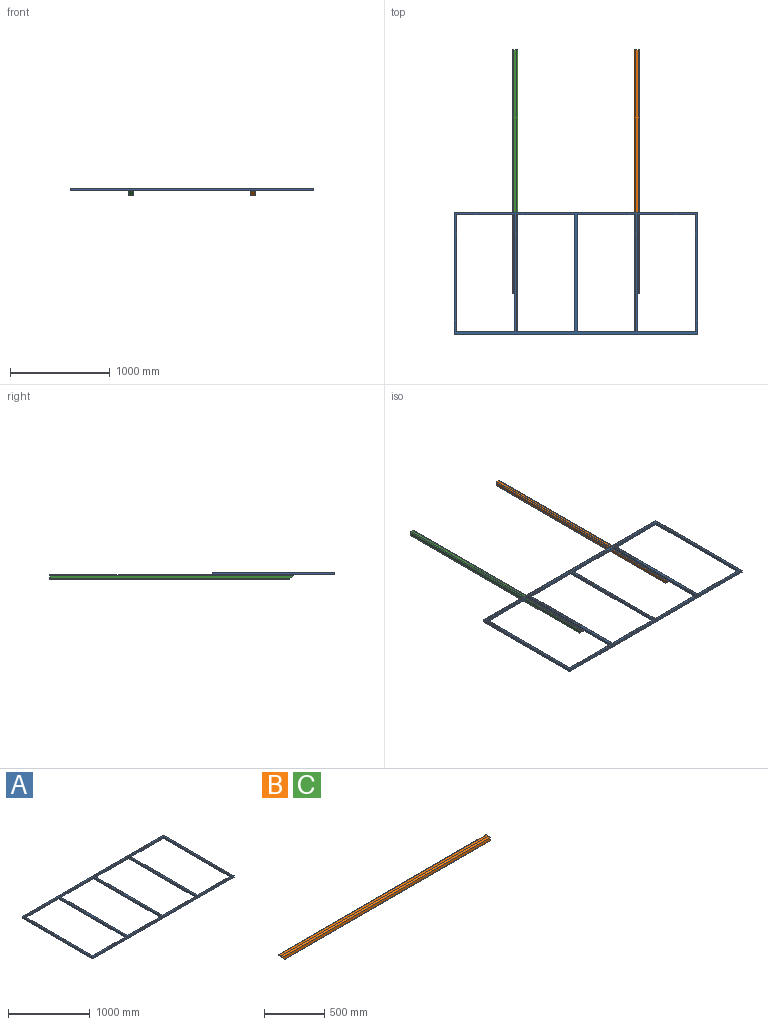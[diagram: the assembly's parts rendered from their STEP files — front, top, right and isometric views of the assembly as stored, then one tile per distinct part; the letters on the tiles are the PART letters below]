
ASSEMBLY  parts=3 mates=2
PART A: 214 faces, bbox 2438.4x1219.2x25.4 mm
  f0: plane 2438.4x22.86mm, normal (0,-1,0), area 55741.8mm2, adj f1,f2,f34,f43
  f1: cylinder r=1.28mm len=2438.4mm, axis (1,0,0), area 4848.5mm2, adj f0,f35,f42,f52
  f2: cylinder r=1.28mm len=2438.4mm, axis (1,0,0), area 4848.5mm2, adj f0,f33,f44,f45
  f3: plane 577.85x22.86mm, normal (0,1,0), area 13209.7mm2, adj f7,f11,f29,f37
  f4: plane 577.85x22.86mm, normal (0,1,0), area 13209.7mm2, adj f8,f12,f32,f40
  f5: plane 577.85x22.86mm, normal (0,1,0), area 13209.7mm2, adj f9,f14,f23,f26
  f6: plane 577.85x22.86mm, normal (0,1,0), area 13209.7mm2, adj f10,f13,f17,f20
  f7: cylinder r=1.28mm len=580.39mm, axis (1,0,0), area 1151.3mm2, adj f3,f28,f36,f52
  f8: cylinder r=1.28mm len=580.39mm, axis (1,0,0), area 1151.3mm2, adj f4,f30,f41,f52
  f9: cylinder r=1.28mm len=580.39mm, axis (1,0,0), area 1151.3mm2, adj f5,f22,f24,f52
  f10: cylinder r=1.28mm len=580.39mm, axis (1,0,0), area 1151.3mm2, adj f6,f16,f18,f52
  f11: cylinder r=1.28mm len=580.39mm, axis (1,0,0), area 1151.3mm2, adj f3,f27,f38,f45
  f12: cylinder r=1.28mm len=580.39mm, axis (1,0,0), area 1151.3mm2, adj f4,f31,f39,f45
  f13: cylinder r=1.28mm len=580.39mm, axis (1,0,0), area 1151.3mm2, adj f6,f15,f19,f45
  f14: cylinder r=1.28mm len=580.39mm, axis (1,0,0), area 1151.3mm2, adj f5,f21,f25,f45
  f15: cylinder r=1.28mm len=1170.94mm, axis (0,-1,0), area 2326mm2, adj f13,f17,f45,f46
  f16: cylinder r=1.28mm len=1170.94mm, axis (0,-1,0), area 2326mm2, adj f10,f17,f47,f52
  f17: plane 1168.4x22.86mm, normal (-1,0,0), area 26709.6mm2, adj f6,f15,f16,f48
  f18: cylinder r=1.28mm len=1170.94mm, axis (0,1,0), area 2326mm2, adj f10,f20,f47,f52
  f19: cylinder r=1.28mm len=1170.94mm, axis (0,1,0), area 2326mm2, adj f13,f20,f45,f46
  f20: plane 1168.4x22.86mm, normal (1,0,0), area 26709.6mm2, adj f6,f18,f19,f48
  f21: cylinder r=1.28mm len=1170.94mm, axis (0,1,0), area 2326mm2, adj f14,f23,f45,f50
  f22: cylinder r=1.28mm len=1170.94mm, axis (0,1,0), area 2326mm2, adj f9,f23,f49,f52
  f23: plane 1168.4x22.86mm, normal (-1,0,0), area 26709.6mm2, adj f5,f21,f22,f51
  f24: cylinder r=1.28mm len=1170.94mm, axis (0,-1,0), area 2326mm2, adj f9,f26,f49,f52
  f25: cylinder r=1.28mm len=1170.94mm, axis (0,-1,0), area 2326mm2, adj f14,f26,f45,f50
  f26: plane 1168.4x22.86mm, normal (1,0,0), area 26709.6mm2, adj f5,f24,f25,f51
  f27: cylinder r=1.28mm len=1170.94mm, axis (0,-1,0), area 2326mm2, adj f11,f29,f45,f53
  f28: cylinder r=1.28mm len=1170.94mm, axis (0,-1,0), area 2326mm2, adj f7,f29,f52,f54
  f29: plane 1168.4x22.86mm, normal (-1,0,0), area 26709.6mm2, adj f3,f27,f28,f55
  f30: cylinder r=1.28mm len=1170.94mm, axis (0,-1,0), area 2326mm2, adj f8,f32,f52,f59
  f31: cylinder r=1.28mm len=1170.94mm, axis (0,-1,0), area 2326mm2, adj f12,f32,f45,f60
  f32: plane 1168.4x22.86mm, normal (1,0,0), area 26709.6mm2, adj f4,f30,f31,f61
  f33: cylinder r=1.28mm len=1219.2mm, axis (0,-1,0), area 2423.3mm2, adj f2,f34,f45,f56
  f34: plane 1219.2x22.86mm, normal (-1,0,0), area 27870.9mm2, adj f0,f33,f35,f57
  f35: cylinder r=1.28mm len=1219.2mm, axis (0,-1,0), area 2423.3mm2, adj f1,f34,f52,f58
  f36: cylinder r=1.28mm len=1170.94mm, axis (0,-1,0), area 2326mm2, adj f7,f37,f52,f54
  f37: plane 1168.4x22.86mm, normal (1,0,0), area 26709.6mm2, adj f3,f36,f38,f55
  f38: cylinder r=1.28mm len=1170.94mm, axis (0,-1,0), area 2326mm2, adj f11,f37,f45,f53
  f39: cylinder r=1.28mm len=1170.94mm, axis (0,1,0), area 2326mm2, adj f12,f40,f45,f60
  f40: plane 1168.4x22.86mm, normal (-1,0,0), area 26709.6mm2, adj f4,f39,f41,f61
  f41: cylinder r=1.28mm len=1170.94mm, axis (0,1,0), area 2326mm2, adj f8,f40,f52,f59
  f42: cylinder r=1.28mm len=1219.2mm, axis (0,1,0), area 2423.3mm2, adj f1,f43,f52,f58
  f43: plane 1219.2x22.86mm, normal (1,0,0), area 27870.9mm2, adj f0,f42,f44,f57
  f44: cylinder r=1.28mm len=1219.2mm, axis (0,1,0), area 2423.3mm2, adj f2,f43,f45,f56
  f45: plane 2435.86x1216.66mm, normal (0,0,-1), area 245206mm2, adj f2,f11,f12,f13,f14,f15,f19,f21
  f46: cylinder r=1.28mm len=580.39mm, axis (-1,0,0), area 1151.3mm2, adj f15,f19,f45,f48
  f47: cylinder r=1.28mm len=580.39mm, axis (-1,0,0), area 1151.3mm2, adj f16,f18,f48,f52
  f48: plane 577.85x22.86mm, normal (0,-1,0), area 13209.7mm2, adj f17,f20,f46,f47
  f49: cylinder r=1.28mm len=580.39mm, axis (-1,0,0), area 1151.3mm2, adj f22,f24,f51,f52
  f50: cylinder r=1.28mm len=580.39mm, axis (-1,0,0), area 1151.3mm2, adj f21,f25,f45,f51
  f51: plane 577.85x22.86mm, normal (0,-1,0), area 13209.7mm2, adj f23,f26,f49,f50
  f52: plane 2435.86x1216.66mm, normal (0,0,1), area 245206mm2, adj f1,f7,f8,f9,f10,f16,f18,f22
  f53: cylinder r=1.28mm len=580.39mm, axis (-1,0,0), area 1151.3mm2, adj f27,f38,f45,f55
  f54: cylinder r=1.28mm len=580.39mm, axis (-1,0,0), area 1151.3mm2, adj f28,f36,f52,f55
  f55: plane 577.85x22.86mm, normal (0,-1,0), area 13209.7mm2, adj f29,f37,f53,f54
  f56: cylinder r=1.28mm len=2438.4mm, axis (-1,0,0), area 4848.5mm2, adj f33,f44,f45,f57
  f57: plane 2438.4x22.86mm, normal (0,1,0), area 55741.8mm2, adj f34,f43,f56,f58
  f58: cylinder r=1.28mm len=2438.4mm, axis (-1,0,0), area 4848.5mm2, adj f35,f42,f52,f57
  f59: cylinder r=1.28mm len=580.39mm, axis (-1,0,0), area 1151.3mm2, adj f30,f41,f52,f61
  f60: cylinder r=1.28mm len=580.39mm, axis (-1,0,0), area 1151.3mm2, adj f31,f39,f45,f61
  f61: plane 577.85x22.86mm, normal (0,-1,0), area 13209.7mm2, adj f32,f40,f59,f60
  f62: plane 21.13x21.13mm, normal (0,1,0), area 445.2mm2, adj f63,f64,f65,f66,f67,f68,f69,f70
  f63: cylinder r=1.28mm len=1168.4mm, axis (0,-1,0), area 2324.1mm2, adj f62,f64,f70,f71
  f64: plane 1168.4x18.59mm, normal (1,0,0), area 21723.8mm2, adj f62,f63,f65,f71
  f65: cylinder r=1.28mm len=1168.4mm, axis (0,-1,0), area 2324.1mm2, adj f62,f64,f66,f71
  f66: plane 1168.4x18.59mm, normal (0,0,-1), area 21723.8mm2, adj f62,f65,f67,f71
  f67: cylinder r=1.28mm len=1168.4mm, axis (0,-1,0), area 2324.1mm2, adj f62,f66,f68,f71
  f68: plane 1168.4x18.59mm, normal (-1,0,0), area 21723.8mm2, adj f62,f67,f69,f71
  f69: cylinder r=1.28mm len=1168.4mm, axis (0,-1,0), area 2324.1mm2, adj f62,f68,f70,f71
  f70: plane 1168.4x18.59mm, normal (0,0,1), area 21723.8mm2, adj f62,f63,f69,f71
  f71: plane 21.13x21.13mm, normal (0,-1,0), area 445.2mm2, adj f63,f64,f65,f66,f67,f68,f69,f70
  f72: plane 21.13x21.13mm, normal (0,1,0), area 445.2mm2, adj f73,f74,f75,f76,f77,f78,f79,f80
  f73: cylinder r=1.28mm len=1168.4mm, axis (0,-1,0), area 2324.1mm2, adj f72,f74,f80,f81
  f74: plane 1168.4x18.59mm, normal (1,0,0), area 21723.8mm2, adj f72,f73,f75,f81
  f75: cylinder r=1.28mm len=1168.4mm, axis (0,-1,0), area 2324.1mm2, adj f72,f74,f76,f81
  f76: plane 1168.4x18.59mm, normal (0,0,-1), area 21723.8mm2, adj f72,f75,f77,f81
  f77: cylinder r=1.28mm len=1168.4mm, axis (0,-1,0), area 2324.1mm2, adj f72,f76,f78,f81
  f78: plane 1168.4x18.59mm, normal (-1,0,0), area 21723.8mm2, adj f72,f77,f79,f81
  f79: cylinder r=1.28mm len=1168.4mm, axis (0,-1,0), area 2324.1mm2, adj f72,f78,f80,f81
  f80: plane 1168.4x18.59mm, normal (0,0,1), area 21723.8mm2, adj f72,f73,f79,f81
  f81: plane 21.13x21.13mm, normal (0,-1,0), area 445.2mm2, adj f73,f74,f75,f76,f77,f78,f79,f80
  f82: plane 21.13x21.13mm, normal (0,1,0), area 445.2mm2, adj f83,f84,f85,f86,f87,f88,f89,f90
  f83: plane 1168.4x18.59mm, normal (0,0,1), area 21723.8mm2, adj f82,f84,f90,f91
  f84: cylinder r=1.28mm len=1168.4mm, axis (0,1,0), area 2324.1mm2, adj f82,f83,f85,f91
  f85: plane 1168.4x18.59mm, normal (1,0,0), area 21723.8mm2, adj f82,f84,f86,f91
  f86: cylinder r=1.28mm len=1168.4mm, axis (0,1,0), area 2324.1mm2, adj f82,f85,f87,f91
  f87: plane 1168.4x18.59mm, normal (0,0,-1), area 21723.8mm2, adj f82,f86,f88,f91
  f88: cylinder r=1.28mm len=1168.4mm, axis (0,1,0), area 2324.1mm2, adj f82,f87,f89,f91
  f89: plane 1168.4x18.59mm, normal (-1,0,0), area 21723.8mm2, adj f82,f88,f90,f91
  f90: cylinder r=1.28mm len=1168.4mm, axis (0,1,0), area 2324.1mm2, adj f82,f83,f89,f91
  f91: plane 21.13x21.13mm, normal (0,-1,0), area 445.2mm2, adj f83,f84,f85,f86,f87,f88,f89,f90
  f92: cylinder r=1.28mm len=1214.93mm, axis (0,1,0), area 2414.9mm2, adj f93,f116,f177,f183
  f93: plane 1214.93x18.59mm, normal (-1,0,0), area 22589mm2, adj f92,f94,f117,f178
  f94: cylinder r=1.28mm len=1214.93mm, axis (0,1,0), area 2414.9mm2, adj f93,f118,f179,f180
  f95: cylinder r=1.28mm len=1175.21mm, axis (0,1,0), area 2334.5mm2, adj f96,f105,f162,f180
  f96: plane 1172.67x18.59mm, normal (1,0,0), area 21803.2mm2, adj f95,f97,f107,f169
  f97: cylinder r=1.28mm len=1175.21mm, axis (0,1,0), area 2334.5mm2, adj f96,f109,f175,f183
  f98: cylinder r=1.28mm len=21.13mm, axis (1,0,0), area 40.2mm2, adj f100,f152,f157,f180
  f99: cylinder r=1.28mm len=577.85mm, axis (1,0,0), area 1149.4mm2, adj f101,f136,f153,f180
  f100: plane 21.13x18.59mm, normal (0,-1,0), area 392.9mm2, adj f98,f102,f151,f156
  f101: plane 577.85x18.59mm, normal (0,-1,0), area 10743.8mm2, adj f99,f103,f136,f153
  f102: cylinder r=1.28mm len=21.13mm, axis (1,0,0), area 40.2mm2, adj f100,f150,f155,f183
  f103: cylinder r=1.28mm len=577.85mm, axis (1,0,0), area 1149.4mm2, adj f101,f136,f153,f183
  f104: cylinder r=1.28mm len=21.13mm, axis (1,0,0), area 40.2mm2, adj f106,f142,f143,f180
  f105: cylinder r=1.28mm len=581.25mm, axis (1,0,0), area 1154.6mm2, adj f95,f107,f147,f180
  f106: plane 21.13x18.59mm, normal (0,-1,0), area 392.9mm2, adj f104,f108,f141,f144
  f107: plane 579.98x18.59mm, normal (0,-1,0), area 10783.5mm2, adj f96,f105,f109,f147
  f108: cylinder r=1.28mm len=21.13mm, axis (1,0,0), area 40.2mm2, adj f106,f140,f145,f183
  f109: cylinder r=1.28mm len=581.25mm, axis (1,0,0), area 1154.6mm2, adj f97,f107,f147,f183
  f110: cylinder r=1.28mm len=21.13mm, axis (1,0,0), area 40.2mm2, adj f112,f132,f133,f180
  f111: cylinder r=1.28mm len=577.85mm, axis (1,0,0), area 1149.4mm2, adj f113,f138,f148,f180
  f112: plane 21.13x18.59mm, normal (0,-1,0), area 392.9mm2, adj f110,f114,f131,f134
  f113: plane 577.85x18.59mm, normal (0,-1,0), area 10743.8mm2, adj f111,f115,f138,f148
  f114: cylinder r=1.28mm len=21.13mm, axis (1,0,0), area 40.2mm2, adj f112,f130,f135,f183
  f115: cylinder r=1.28mm len=577.85mm, axis (1,0,0), area 1149.4mm2, adj f113,f138,f148,f183
  f116: cylinder r=1.28mm len=2434.13mm, axis (1,0,0), area 4840.1mm2, adj f92,f117,f122,f183
  f117: plane 2434.13x18.59mm, normal (0,1,0), area 45257.3mm2, adj f93,f116,f118,f123
  f118: cylinder r=1.28mm len=2434.13mm, axis (1,0,0), area 4840.1mm2, adj f94,f117,f124,f180
  f119: cylinder r=1.28mm len=581.25mm, axis (1,0,0), area 1154.6mm2, adj f120,f125,f128,f180
  f120: plane 579.98x18.59mm, normal (0,-1,0), area 10783.5mm2, adj f119,f121,f126,f128
  f121: cylinder r=1.28mm len=581.25mm, axis (1,0,0), area 1154.6mm2, adj f120,f127,f128,f183
  f122: cylinder r=1.28mm len=1214.93mm, axis (0,-1,0), area 2414.9mm2, adj f116,f123,f177,f183
  f123: plane 1214.93x18.59mm, normal (1,0,0), area 22589mm2, adj f117,f122,f124,f178
  f124: cylinder r=1.28mm len=1214.93mm, axis (0,-1,0), area 2414.9mm2, adj f118,f123,f179,f180
  f125: cylinder r=1.28mm len=1175.21mm, axis (0,-1,0), area 2334.5mm2, adj f119,f126,f159,f180
  f126: plane 1172.67x18.59mm, normal (-1,0,0), area 21803.2mm2, adj f120,f125,f127,f164
  f127: cylinder r=1.28mm len=1175.21mm, axis (0,-1,0), area 2334.5mm2, adj f121,f126,f172,f183
  f128: plane 21.13x10.57mm, normal (-1,0,0), area 222.6mm2, adj f119,f120,f121,f129,f180,f183
  f129: plane 21.13x3.4mm, normal (0,-1,0), area 45.8mm2, adj f128,f130,f131,f132,f180,f183
  f130: cylinder r=1.28mm len=10.57mm, axis (0,-1,0), area 20.1mm2, adj f114,f129,f131,f183
  f131: plane 18.59x10.57mm, normal (1,0,0), area 196.5mm2, adj f112,f129,f130,f132
  f132: cylinder r=1.28mm len=10.57mm, axis (0,-1,0), area 20.1mm2, adj f110,f129,f131,f180
  f133: cylinder r=1.28mm len=10.57mm, axis (0,-1,0), area 20.1mm2, adj f110,f134,f137,f180
  f134: plane 18.59x10.57mm, normal (-1,0,0), area 196.5mm2, adj f112,f133,f135,f137
  f135: cylinder r=1.28mm len=10.57mm, axis (0,-1,0), area 20.1mm2, adj f114,f134,f137,f183
  f136: plane 21.13x10.57mm, normal (1,0,0), area 222.6mm2, adj f99,f101,f103,f137,f180,f183
  f137: plane 21.13x3.4mm, normal (0,-1,0), area 45.8mm2, adj f133,f134,f135,f136,f180,f183
  f138: plane 21.13x10.57mm, normal (-1,0,0), area 222.6mm2, adj f111,f113,f115,f139,f180,f183
  f139: plane 21.13x3.4mm, normal (0,-1,0), area 45.8mm2, adj f138,f140,f141,f142,f180,f183
  f140: cylinder r=1.28mm len=10.57mm, axis (0,-1,0), area 20.1mm2, adj f108,f139,f141,f183
  f141: plane 18.59x10.57mm, normal (1,0,0), area 196.5mm2, adj f106,f139,f140,f142
  f142: cylinder r=1.28mm len=10.57mm, axis (0,-1,0), area 20.1mm2, adj f104,f139,f141,f180
  f143: cylinder r=1.28mm len=10.57mm, axis (0,-1,0), area 20.1mm2, adj f104,f144,f146,f180
  f144: plane 18.59x10.57mm, normal (-1,0,0), area 196.5mm2, adj f106,f143,f145,f146
  f145: cylinder r=1.28mm len=10.57mm, axis (0,-1,0), area 20.1mm2, adj f108,f144,f146,f183
  f146: plane 21.13x3.4mm, normal (0,-1,0), area 45.8mm2, adj f143,f144,f145,f147,f180,f183
  f147: plane 21.13x10.57mm, normal (1,0,0), area 222.6mm2, adj f105,f107,f109,f146,f180,f183
  f148: plane 21.13x10.57mm, normal (1,0,0), area 222.6mm2, adj f111,f113,f115,f149,f180,f183
  f149: plane 21.13x3.4mm, normal (0,-1,0), area 45.8mm2, adj f148,f150,f151,f152,f180,f183
  f150: cylinder r=1.28mm len=10.57mm, axis (0,1,0), area 20.1mm2, adj f102,f149,f151,f183
  f151: plane 18.59x10.57mm, normal (-1,0,0), area 196.5mm2, adj f100,f149,f150,f152
  f152: cylinder r=1.28mm len=10.57mm, axis (0,1,0), area 20.1mm2, adj f98,f149,f151,f180
  f153: plane 21.13x10.57mm, normal (-1,0,0), area 222.6mm2, adj f99,f101,f103,f154,f180,f183
  f154: plane 21.13x3.4mm, normal (0,-1,0), area 45.8mm2, adj f153,f155,f156,f157,f180,f183
  f155: cylinder r=1.28mm len=10.57mm, axis (0,1,0), area 20.1mm2, adj f102,f154,f156,f183
  f156: plane 18.59x10.57mm, normal (1,0,0), area 196.5mm2, adj f100,f154,f155,f157
  f157: cylinder r=1.28mm len=10.57mm, axis (0,1,0), area 20.1mm2, adj f98,f154,f156,f180
  f158: cylinder r=1.28mm len=577.85mm, axis (-1,0,0), area 1149.4mm2, adj f165,f180,f190,f210
  f159: cylinder r=1.28mm len=581.25mm, axis (-1,0,0), area 1154.6mm2, adj f125,f164,f180,f205
  f160: cylinder r=1.28mm len=21.13mm, axis (-1,0,0), area 40.2mm2, adj f167,f180,f198,f203
  f161: cylinder r=1.28mm len=577.85mm, axis (-1,0,0), area 1149.4mm2, adj f168,f180,f185,f199
  f162: cylinder r=1.28mm len=581.25mm, axis (-1,0,0), area 1154.6mm2, adj f95,f169,f180,f194
  f163: cylinder r=1.28mm len=21.13mm, axis (-1,0,0), area 40.2mm2, adj f166,f180,f208,f213
  f164: plane 579.98x18.59mm, normal (0,1,0), area 10783.5mm2, adj f126,f159,f172,f205
  f165: plane 577.85x18.59mm, normal (0,1,0), area 10743.8mm2, adj f158,f171,f190,f210
  f166: plane 21.13x18.59mm, normal (0,1,0), area 392.9mm2, adj f163,f176,f207,f212
  f167: plane 21.13x18.59mm, normal (0,1,0), area 392.9mm2, adj f160,f173,f197,f202
  f168: plane 577.85x18.59mm, normal (0,1,0), area 10743.8mm2, adj f161,f174,f185,f199
  f169: plane 579.98x18.59mm, normal (0,1,0), area 10783.5mm2, adj f96,f162,f175,f194
  f170: plane 21.13x18.59mm, normal (0,1,0), area 392.9mm2, adj f181,f182,f187,f192
  f171: cylinder r=1.28mm len=577.85mm, axis (-1,0,0), area 1149.4mm2, adj f165,f183,f190,f210
  f172: cylinder r=1.28mm len=581.25mm, axis (-1,0,0), area 1154.6mm2, adj f127,f164,f183,f205
  f173: cylinder r=1.28mm len=21.13mm, axis (-1,0,0), area 40.2mm2, adj f167,f183,f196,f201
  f174: cylinder r=1.28mm len=577.85mm, axis (-1,0,0), area 1149.4mm2, adj f168,f183,f185,f199
  f175: cylinder r=1.28mm len=581.25mm, axis (-1,0,0), area 1154.6mm2, adj f97,f169,f183,f194
  f176: cylinder r=1.28mm len=21.13mm, axis (-1,0,0), area 40.2mm2, adj f166,f183,f206,f211
  f177: cylinder r=1.28mm len=2434.13mm, axis (-1,0,0), area 4840.1mm2, adj f92,f122,f178,f183
  f178: plane 2434.13x18.59mm, normal (0,-1,0), area 45257.3mm2, adj f93,f123,f177,f179
  f179: cylinder r=1.28mm len=2434.13mm, axis (-1,0,0), area 4840.1mm2, adj f94,f124,f178,f180
  f180: plane 2431.59x1212.39mm, normal (0,0,-1), area 133741.3mm2, adj f94,f95,f98,f99,f104,f105,f110,f111
  f181: cylinder r=1.28mm len=21.13mm, axis (-1,0,0), area 40.2mm2, adj f170,f180,f188,f193
  f182: cylinder r=1.28mm len=21.13mm, axis (-1,0,0), area 40.2mm2, adj f170,f183,f186,f191
  f183: plane 2431.59x1212.39mm, normal (0,0,1), area 133741.3mm2, adj f92,f97,f102,f103,f108,f109,f114,f115
  f184: plane 21.13x3.4mm, normal (0,1,0), area 45.8mm2, adj f180,f183,f185,f186,f187,f188
  f185: plane 21.13x10.57mm, normal (1,0,0), area 222.6mm2, adj f161,f168,f174,f180,f183,f184
  f186: cylinder r=1.28mm len=10.57mm, axis (0,1,0), area 20.1mm2, adj f182,f183,f184,f187
  f187: plane 18.59x10.57mm, normal (-1,0,0), area 196.5mm2, adj f170,f184,f186,f188
  f188: cylinder r=1.28mm len=10.57mm, axis (0,1,0), area 20.1mm2, adj f180,f181,f184,f187
  f189: plane 21.13x3.4mm, normal (0,1,0), area 45.8mm2, adj f180,f183,f190,f191,f192,f193
  f190: plane 21.13x10.57mm, normal (-1,0,0), area 222.6mm2, adj f158,f165,f171,f180,f183,f189
  f191: cylinder r=1.28mm len=10.57mm, axis (0,1,0), area 20.1mm2, adj f182,f183,f189,f192
  f192: plane 18.59x10.57mm, normal (1,0,0), area 196.5mm2, adj f170,f189,f191,f193
  f193: cylinder r=1.28mm len=10.57mm, axis (0,1,0), area 20.1mm2, adj f180,f181,f189,f192
  f194: plane 21.13x10.57mm, normal (1,0,0), area 222.6mm2, adj f162,f169,f175,f180,f183,f195
  f195: plane 21.13x3.4mm, normal (0,1,0), area 45.8mm2, adj f180,f183,f194,f196,f197,f198
  f196: cylinder r=1.28mm len=10.57mm, axis (0,-1,0), area 20.1mm2, adj f173,f183,f195,f197
  f197: plane 18.59x10.57mm, normal (-1,0,0), area 196.5mm2, adj f167,f195,f196,f198
  f198: cylinder r=1.28mm len=10.57mm, axis (0,-1,0), area 20.1mm2, adj f160,f180,f195,f197
  f199: plane 21.13x10.57mm, normal (-1,0,0), area 222.6mm2, adj f161,f168,f174,f180,f183,f200
  f200: plane 21.13x3.4mm, normal (0,1,0), area 45.8mm2, adj f180,f183,f199,f201,f202,f203
  f201: cylinder r=1.28mm len=10.57mm, axis (0,-1,0), area 20.1mm2, adj f173,f183,f200,f202
  f202: plane 18.59x10.57mm, normal (1,0,0), area 196.5mm2, adj f167,f200,f201,f203
  f203: cylinder r=1.28mm len=10.57mm, axis (0,-1,0), area 20.1mm2, adj f160,f180,f200,f202
  f204: plane 21.13x3.4mm, normal (0,1,0), area 45.8mm2, adj f180,f183,f205,f206,f207,f208
  f205: plane 21.13x10.57mm, normal (-1,0,0), area 222.6mm2, adj f159,f164,f172,f180,f183,f204
  f206: cylinder r=1.28mm len=10.57mm, axis (0,-1,0), area 20.1mm2, adj f176,f183,f204,f207
  f207: plane 18.59x10.57mm, normal (1,0,0), area 196.5mm2, adj f166,f204,f206,f208
  f208: cylinder r=1.28mm len=10.57mm, axis (0,-1,0), area 20.1mm2, adj f163,f180,f204,f207
  f209: plane 21.13x3.4mm, normal (0,1,0), area 45.8mm2, adj f180,f183,f210,f211,f212,f213
  f210: plane 21.13x10.57mm, normal (1,0,0), area 222.6mm2, adj f158,f165,f171,f180,f183,f209
  f211: cylinder r=1.28mm len=10.57mm, axis (0,-1,0), area 20.1mm2, adj f176,f183,f209,f212
  f212: plane 18.59x10.57mm, normal (-1,0,0), area 196.5mm2, adj f166,f209,f211,f213
  f213: cylinder r=1.28mm len=10.57mm, axis (0,-1,0), area 20.1mm2, adj f163,f180,f209,f212
PART B: 26 faces, bbox 2442x50.8x52.6 mm
  f0: plane 2429.23x27.21mm, normal (0,-1,0), area 61423.9mm2, adj f1,f7,f12,f13,f14,f15
  f1: cylinder r=12.7mm len=2440.21mm, axis (-1,0,0), area 48591.7mm2, adj f0,f2,f13,f15
  f2: plane 2440.21x25.4mm, normal (0,0,1), area 61981.4mm2, adj f1,f3,f8,f15
  f3: cylinder r=12.7mm len=2440.21mm, axis (-1,0,0), area 48591.7mm2, adj f2,f4,f9,f15
  f4: plane 2429.23x27.2mm, normal (0,1,0), area 61423.8mm2, adj f3,f5,f9,f10,f14,f15
  f5: cylinder r=12.7mm len=2401.88mm, axis (-1,0,0), area 47757.3mm2, adj f4,f6,f10,f15
  f6: plane 2389.11x25.4mm, normal (0,0,-1), area 60683.3mm2, adj f5,f7,f11,f15
  f7: cylinder r=12.7mm len=2401.88mm, axis (-1,0,0), area 47757.3mm2, adj f0,f6,f12,f15
  f8: plane 25.4x1.8mm, normal (-0.71,0,0.7), area 64.5mm2, adj f2,f9,f13,f14
  f9: extruded ~14.57x14.5mm, area 61.7mm2, adj f3,f4,f8,f14
  f10: extruded ~14.57x14.5mm, area 61.7mm2, adj f4,f5,f11,f14
  f11: plane 25.4x1.8mm, normal (0.71,0,-0.7), area 64.5mm2, adj f6,f10,f12,f14
  f12: extruded ~14.57x14.5mm, area 61.7mm2, adj f0,f7,f11,f14
  f13: extruded ~14.56x14.5mm, area 61.7mm2, adj f0,f1,f8,f14
  f14: plane 51.11x50.8mm, normal (-0.7,0,-0.71), area 3464.3mm2, adj f0,f4,f8,f9,f10,f11,f12,f13
  f15: plane 50.8x50.8mm, normal (1,0,0), area 2442.3mm2, adj f0,f1,f2,f3,f4,f5,f6,f7
  f16: plane 38.33x38.1mm, normal (0.7,0,0.71), area 2010mm2, adj f17,f18,f19,f20,f21,f22,f23,f24
  f17: cylinder r=6.35mm len=2399.34mm, axis (-1,0,0), area 23893.9mm2, adj f16,f18,f24,f25
  f18: plane 2392.95x25.4mm, normal (0,0,1), area 60781mm2, adj f16,f17,f19,f25
  f19: cylinder r=6.35mm len=2399.34mm, axis (-1,0,0), area 23893.9mm2, adj f16,f18,f20,f25
  f20: plane 2424.9x25.4mm, normal (0,-1,0), area 61267.8mm2, adj f16,f19,f21,f25
  f21: cylinder r=6.35mm len=2431.28mm, axis (-1,0,0), area 24229.9mm2, adj f16,f20,f22,f25
  f22: plane 2431.28x25.4mm, normal (0,0,-1), area 61754.6mm2, adj f16,f21,f23,f25
  f23: cylinder r=6.35mm len=2431.28mm, axis (-1,0,0), area 24229.9mm2, adj f16,f22,f24,f25
  f24: plane 2424.9x25.4mm, normal (0,1,0), area 61267.8mm2, adj f16,f17,f23,f25
  f25: plane 38.1x38.1mm, normal (-1,0,0), area 1417mm2, adj f17,f18,f19,f20,f21,f22,f23,f24
PART C: same geometry as B
PLACE A t=(-196.15,-55.52,86.59)mm
PLACE B rot(axis=(0,0,1),90deg) t=(413.45,2180.23,48.49)mm
PLACE C rot(axis=(0,0,1),90deg) t=(-805.75,2180.23,48.49)mm
MATE fastened B.f2 <-> A.f45  axis (0,0,1) through (413.45,-257.45,73.89)mm
MATE fastened C.f2 <-> A.f45  axis (0,0,1) through (-805.75,-257.45,73.89)mm
